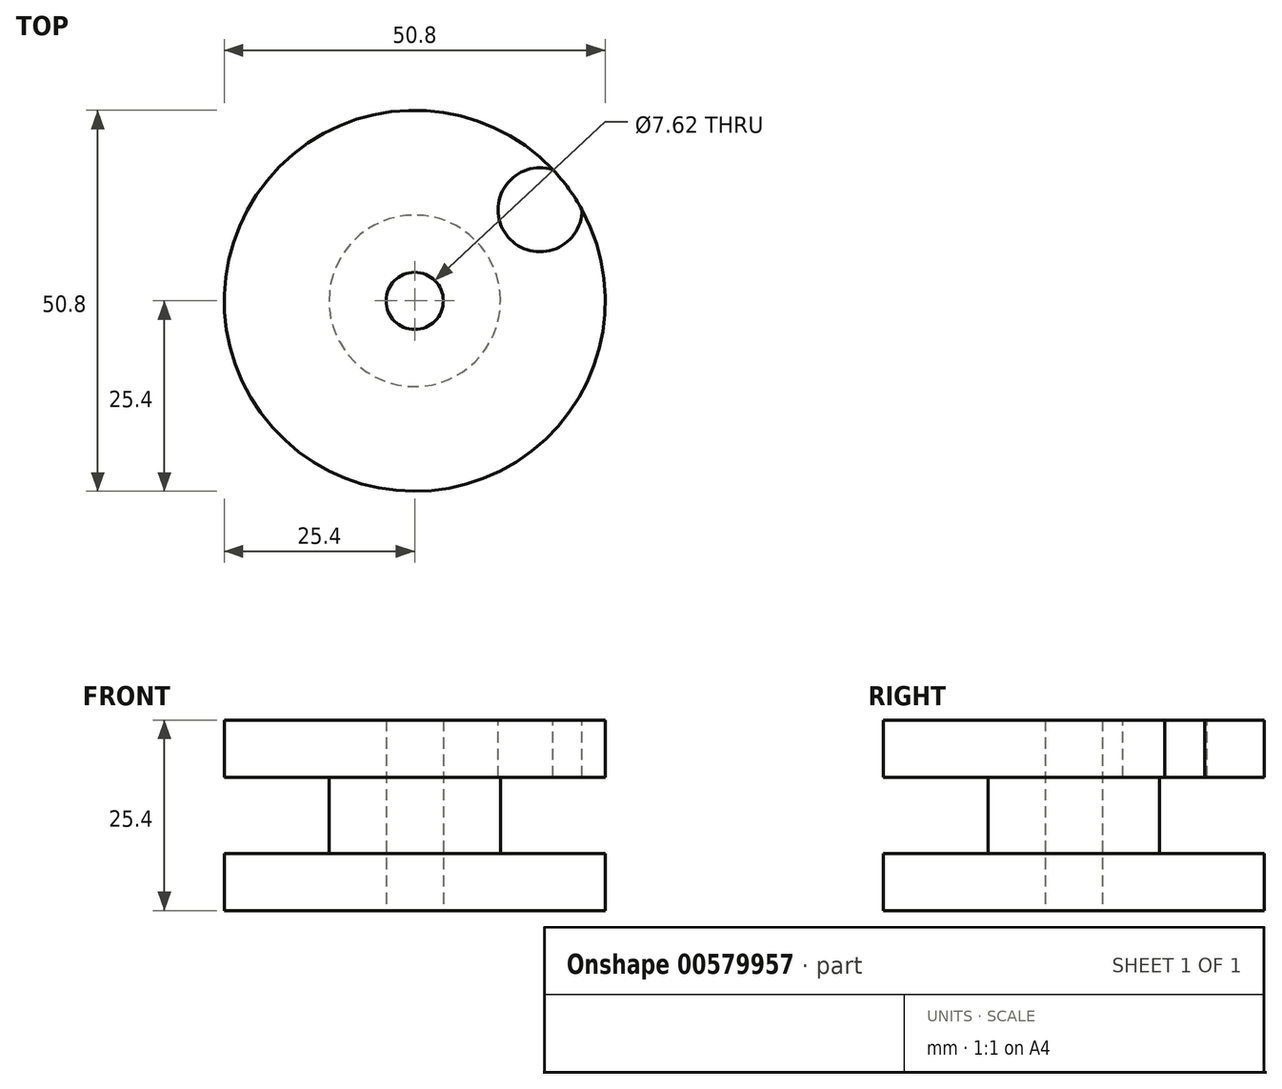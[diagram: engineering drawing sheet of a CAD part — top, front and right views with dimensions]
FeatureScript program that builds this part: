
annotation { "Feature Type Name" : "Feature", "Feature Type Description" : "" }
export const myFeature = defineFeature(function(context is Context, id is Id, definition is map)
    precondition{}
    {
        {
            var Q0;
            Q0=qCreatedBy(makeId("Top.planeOp"),FACE);
            var sketch = newSketch(context, id + "F0", { "sketchPlane" : qUnion([Q0])});
            skCircle(sketch, "E0", {"center": v(0, 0) * mm, "radius": 25.4 * mm});
            skArc(sketch, "E1", {"start": v(13.01, 21.81) * mm, "mid": v(7.75, 9.74) * mm, "end": v(18.35, 17.57) * mm});
            skCircle(sketch, "E2", {"center": v(0, 0) * mm, "radius": 3.81 * mm});
            skSolve(sketch);
        }
        {
            var Q0;
            {var subQ0=sQuery(id+"F0.wireOp",EDGE,"E1");Q0=makeQuery(id+"F0.imprint","IMPRINT",FACE,{"disambiguationData":[TD([[makeQuery(id+"F0.imprint","IMPRINT",EDGE,{"derivedFrom":subQ0}),-1.0]])]});}
            var Q1;
            {var subQ0=sQuery(id+"F0.wireOp",EDGE,"E1");Q1=makeQuery(id+"F0.imprint","IMPRINT",FACE,{"disambiguationData":[TD([[makeQuery(id+"F0.imprint","IMPRINT",EDGE,{"derivedFrom":subQ0}),1.0]])]});}
            extrude(context, id + "F1", {"entities" : qUnion([Q0, Q1]), "depth" : 12.7 * mm, "offsetDistance" : 25.4 * mm});
        }
        {
            var Q0;
            Q0=makeQuery(id+"F1.opExtrude","CAP_FACE",FACE,{"disambiguationData":[OSD([sQuery(id+"F0.wireOp",EDGE,"E0"),sQuery(id+"F0.wireOp",EDGE,"E2")])],"isStart":false});
            extrude(context, id + "F2", {"entities" : qUnion([Q0]), "operationType" : NewBodyOperationType.ADD, "depth" : 12.7 * mm, "offsetDistance" : 25.4 * mm});
        }
        {
            var Q0;
            {var subQ0=sQuery(id+"F0.wireOp",EDGE,"E0");Q0=makeQuery(id+"F2.boolean.opBoolean","MERGE",FACE,{"derivedFrom":[makeQuery(id+"F1.opExtrude","SWEPT_FACE",FACE,{"disambiguationData":[OSD([subQ0])]}),makeQuery(id+"F2.opExtrude","SWEPT_FACE",FACE,{"disambiguationData":[OSD([subQ0])]})]});}
            shell(context, id + "F3", {"entities" : qUnion([Q0]), "thickness" : 7.62 * mm});
        }
        {
            var Q0;
            Q0=makeQuery(id+"F2.opExtrude","CAP_FACE",FACE,{"disambiguationData":[OSD([sQuery(id+"F0.wireOp",EDGE,"E0"),sQuery(id+"F0.wireOp",EDGE,"E2")])],"isStart":false});
            var sketch = newSketch(context, id + "F4", { "sketchPlane" : qUnion([Q0])});
            skArc(sketch, "E3", {"start": v(18.43, 17.47) * mm, "mid": v(12.18, 8.85) * mm, "end": v(22.32, 12.13) * mm});
            skSolve(sketch);
        }
        {
            var Q0;
            {var subQ0=sQuery(id+"F4.wireOp",EDGE,"E3");Q0=makeQuery(id+"F4.imprint","IMPRINT",FACE,{"disambiguationData":[TD([[makeQuery(id+"F4.imprint","IMPRINT",EDGE,{"derivedFrom":subQ0}),1.0]])]});}
            extrude(context, id + "F5", {"entities" : qUnion([Q0]), "operationType" : NewBodyOperationType.REMOVE, "oppositeDirection" : true, "depth" : 10.16 * mm, "offsetDistance" : 25.4 * mm});
        }
    });
